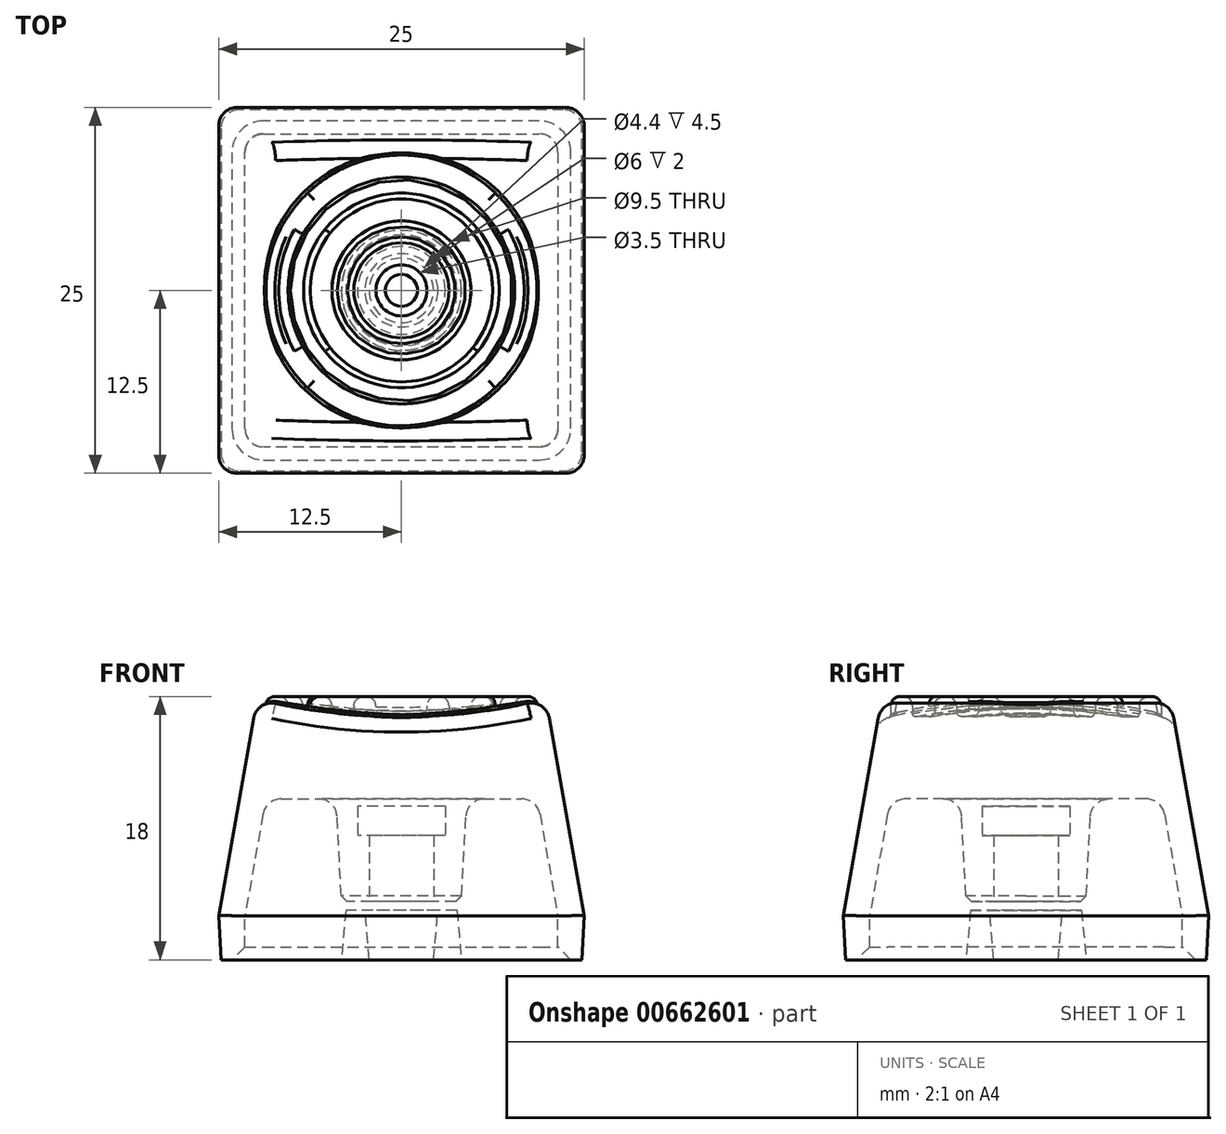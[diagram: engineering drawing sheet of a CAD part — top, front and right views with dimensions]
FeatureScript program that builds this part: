
annotation { "Feature Type Name" : "Feature", "Feature Type Description" : "" }
export const myFeature = defineFeature(function(context is Context, id is Id, definition is map)
    precondition{}
    {
        {
            var Q0;
            Q0=qCreatedBy(makeId("Top.planeOp"),FACE);
            var sketch = newSketch(context, id + "F0", { "sketchPlane" : qUnion([Q0])});
            skLineSegment(sketch, "E0.bottom", {"start": v(12.5, 12.5) * mm, "end": v(-12.5, 12.5) * mm});
            skLineSegment(sketch, "E0.top", {"start": v(12.5, -12.5) * mm, "end": v(-12.5, -12.5) * mm});
            skLineSegment(sketch, "E0.left", {"start": v(12.5, 12.5) * mm, "end": v(12.5, -12.5) * mm});
            skLineSegment(sketch, "E0.right", {"start": v(-12.5, 12.5) * mm, "end": v(-12.5, -12.5) * mm});
            skPoint(sketch, "E0.middle", {"position": v(0, 0) * mm});
            skPoint(sketch, "E1.right.end.orphan", {"position": v(-19.05, 19.05) * mm});
            skPoint(sketch, "E1.bottom.end.orphan", {"position": v(-19.05, -19.05) * mm});
            skPoint(sketch, "E1.left.end.orphan", {"position": v(19.05, 19.05) * mm});
            skPoint(sketch, "E1.left.start.orphan", {"position": v(19.05, -19.05) * mm});
            skSolve(sketch);
        }
        {
            var Q0;
            Q0=qSketchRegion(id+"F0",true);
            extrude(context, id + "F1", {"entities" : qUnion([Q0]), "depth" : 15 * mm, "offsetDistance" : 25.4 * mm, "hasDraft" : true, "draftAngle" : 10 * degree, "draftPullDirection" : true});
        }
        {
            var Q0;
            Q0=qCreatedBy(makeId("Top.planeOp"),FACE);
            var sketch = newSketch(context, id + "F2", { "sketchPlane" : qUnion([Q0])});
            skLineSegment(sketch, "E2.bottom", {"start": v(10.7, 10.7) * mm, "end": v(-10.7, 10.7) * mm});
            skLineSegment(sketch, "E2.top", {"start": v(10.7, -10.7) * mm, "end": v(-10.7, -10.7) * mm});
            skLineSegment(sketch, "E2.left", {"start": v(10.7, 10.7) * mm, "end": v(10.7, -10.7) * mm});
            skLineSegment(sketch, "E2.right", {"start": v(-10.7, 10.7) * mm, "end": v(-10.7, -10.7) * mm});
            skPoint(sketch, "E2.middle", {"position": v(0, 0) * mm});
            skSolve(sketch);
        }
        {
            var Q0;
            Q0=qSketchRegion(id+"F2",true);
            extrude(context, id + "F3", {"entities" : qUnion([Q0]), "operationType" : NewBodyOperationType.REMOVE, "depth" : 8 * mm, "offsetDistance" : 25.4 * mm, "hasDraft" : true, "draftAngle" : 10 * degree, "draftPullDirection" : true});
        }
        {
            var Q0;
            Q0=makeQuery(id+"F3.boolean.opBoolean","COPY",EDGE,{"derivedFrom":makeQuery(id+"F3.opExtrude","CAP_EDGE",EDGE,{"disambiguationData":[OSD([sQuery(id+"F2.wireOp",EDGE,"E2.bottom")])],"isStart":false})});
            var Q1;
            Q1=makeQuery(id+"F3.boolean.opBoolean","COPY",EDGE,{"derivedFrom":makeQuery(id+"F3.opExtrude","CAP_EDGE",EDGE,{"disambiguationData":[OSD([sQuery(id+"F2.wireOp",EDGE,"E2.right")])],"isStart":false})});
            var Q2;
            Q2=makeQuery(id+"F3.boolean.opBoolean","COPY",EDGE,{"derivedFrom":makeQuery(id+"F3.opExtrude","CAP_EDGE",EDGE,{"disambiguationData":[OSD([sQuery(id+"F2.wireOp",EDGE,"E2.top")])],"isStart":false})});
            var Q3;
            Q3=makeQuery(id+"F3.boolean.opBoolean","COPY",EDGE,{"derivedFrom":makeQuery(id+"F3.opExtrude","CAP_EDGE",EDGE,{"disambiguationData":[OSD([sQuery(id+"F2.wireOp",EDGE,"E2.left")])],"isStart":false})});
            fillet(context, id + "F4", {"entities" : qUnion([Q0, Q1, Q2, Q3]), "radius" : 1.27 * mm, "tangentPropagation" : true, "allowEdgeOverflow" : false});
        }
        {
            var Q0;
            Q0=makeQuery(id+"F4.opFillet","BLEND_EDGE",EDGE,{"blendedFrom":[makeQuery(id+"F3.boolean.opBoolean","COPY",EDGE,{"derivedFrom":makeQuery(id+"F3.opExtrude","CAP_EDGE",EDGE,{"disambiguationData":[OSD([sQuery(id+"F2.wireOp",EDGE,"E2.bottom")])],"isStart":false})}),makeQuery(id+"F3.boolean.opBoolean","COPY",EDGE,{"derivedFrom":makeQuery(id+"F3.opExtrude","CAP_EDGE",EDGE,{"disambiguationData":[OSD([sQuery(id+"F2.wireOp",EDGE,"E2.right")])],"isStart":false})})],"blendedInto":[]});
            var Q1;
            Q1=makeQuery(id+"F4.opFillet","BLEND_EDGE",EDGE,{"blendedFrom":[makeQuery(id+"F3.boolean.opBoolean","COPY",EDGE,{"derivedFrom":makeQuery(id+"F3.opExtrude","CAP_EDGE",EDGE,{"disambiguationData":[OSD([sQuery(id+"F2.wireOp",EDGE,"E2.bottom")])],"isStart":false})}),makeQuery(id+"F3.boolean.opBoolean","COPY",EDGE,{"derivedFrom":makeQuery(id+"F3.opExtrude","CAP_EDGE",EDGE,{"disambiguationData":[OSD([sQuery(id+"F2.wireOp",EDGE,"E2.left")])],"isStart":false})})],"blendedInto":[]});
            var Q2;
            Q2=makeQuery(id+"F4.opFillet","BLEND_EDGE",EDGE,{"blendedFrom":[makeQuery(id+"F3.boolean.opBoolean","COPY",EDGE,{"derivedFrom":makeQuery(id+"F3.opExtrude","CAP_EDGE",EDGE,{"disambiguationData":[OSD([sQuery(id+"F2.wireOp",EDGE,"E2.top")])],"isStart":false})}),makeQuery(id+"F3.boolean.opBoolean","COPY",EDGE,{"derivedFrom":makeQuery(id+"F3.opExtrude","CAP_EDGE",EDGE,{"disambiguationData":[OSD([sQuery(id+"F2.wireOp",EDGE,"E2.left")])],"isStart":false})})],"blendedInto":[]});
            var Q3;
            Q3=makeQuery(id+"F4.opFillet","BLEND_EDGE",EDGE,{"blendedFrom":[makeQuery(id+"F3.boolean.opBoolean","COPY",EDGE,{"derivedFrom":makeQuery(id+"F3.opExtrude","CAP_EDGE",EDGE,{"disambiguationData":[OSD([sQuery(id+"F2.wireOp",EDGE,"E2.top")])],"isStart":false})}),makeQuery(id+"F3.boolean.opBoolean","COPY",EDGE,{"derivedFrom":makeQuery(id+"F3.opExtrude","CAP_EDGE",EDGE,{"disambiguationData":[OSD([sQuery(id+"F2.wireOp",EDGE,"E2.right")])],"isStart":false})})],"blendedInto":[]});
            fillet(context, id + "F5", {"entities" : qUnion([Q0, Q1, Q2, Q3]), "radius" : 1.27 * mm, "tangentPropagation" : true, "allowEdgeOverflow" : false});
        }
        {
            var Q0;
            Q0=makeQuery(id+"F0.imprint","IMPRINT",FACE,{"disambiguationData":[TD([[makeQuery(id+"F0.imprint","IMPRINT",EDGE,{"derivedFrom":sQuery(id+"F0.wireOp",EDGE,"E0.bottom")}),1.0]])]});
            extrude(context, id + "F6", {"entities" : qUnion([Q0]), "operationType" : NewBodyOperationType.ADD, "oppositeDirection" : true, "depth" : 3 * mm, "offsetDistance" : 25.4 * mm, "hasDraft" : true, "draftAngle" : 3 * degree, "draftPullDirection" : true});
        }
        {
            var Q0;
            Q0=makeQuery(id+"F2.imprint","IMPRINT",FACE,{"disambiguationData":[TD([[makeQuery(id+"F2.imprint","IMPRINT",EDGE,{"derivedFrom":sQuery(id+"F2.wireOp",EDGE,"E2.bottom")}),1.0]])]});
            extrude(context, id + "F7", {"entities" : qUnion([Q0]), "operationType" : NewBodyOperationType.REMOVE, "oppositeDirection" : true, "depth" : 25.4 * mm, "offsetDistance" : 25.4 * mm});
        }
        {
            var Q0;
            Q0=makeQuery(id+"F7.boolean.opBoolean","COPY",EDGE,{"derivedFrom":makeQuery(id+"F7.opExtrude","SWEPT_EDGE",EDGE,{"disambiguationData":[OSD([sQuery(id+"F2.wireOp",EDGE,"E2.bottom"),sQuery(id+"F2.wireOp",EDGE,"E2.right")])]})});
            var Q1;
            Q1=makeQuery(id+"F7.boolean.opBoolean","COPY",EDGE,{"derivedFrom":makeQuery(id+"F7.opExtrude","SWEPT_EDGE",EDGE,{"disambiguationData":[OSD([sQuery(id+"F2.wireOp",EDGE,"E2.top"),sQuery(id+"F2.wireOp",EDGE,"E2.right")])]})});
            var Q2;
            Q2=makeQuery(id+"F7.boolean.opBoolean","COPY",EDGE,{"derivedFrom":makeQuery(id+"F7.opExtrude","SWEPT_EDGE",EDGE,{"disambiguationData":[OSD([sQuery(id+"F2.wireOp",EDGE,"E2.bottom"),sQuery(id+"F2.wireOp",EDGE,"E2.left")])]})});
            var Q3;
            Q3=makeQuery(id+"F7.boolean.opBoolean","COPY",EDGE,{"derivedFrom":makeQuery(id+"F7.opExtrude","SWEPT_EDGE",EDGE,{"disambiguationData":[OSD([sQuery(id+"F2.wireOp",EDGE,"E2.top"),sQuery(id+"F2.wireOp",EDGE,"E2.left")])]})});
            fillet(context, id + "F8", {"entities" : qUnion([Q0, Q1, Q2, Q3]), "radius" : 1.27 * mm, "tangentPropagation" : true, "allowEdgeOverflow" : false});
        }
        {
            var Q0;
            Q0=makeQuery(id+"F6.opExtrude","SWEPT_EDGE",EDGE,{"disambiguationData":[OSD([sQuery(id+"F0.wireOp",EDGE,"E0.bottom"),sQuery(id+"F0.wireOp",EDGE,"E0.right")])]});
            var Q1;
            Q1=makeQuery(id+"F6.opExtrude","SWEPT_EDGE",EDGE,{"disambiguationData":[OSD([sQuery(id+"F0.wireOp",EDGE,"E0.bottom"),sQuery(id+"F0.wireOp",EDGE,"E0.left")])]});
            var Q2;
            Q2=makeQuery(id+"F6.opExtrude","SWEPT_EDGE",EDGE,{"disambiguationData":[OSD([sQuery(id+"F0.wireOp",EDGE,"E0.top"),sQuery(id+"F0.wireOp",EDGE,"E0.right")])]});
            var Q3;
            Q3=makeQuery(id+"F6.opExtrude","SWEPT_EDGE",EDGE,{"disambiguationData":[OSD([sQuery(id+"F0.wireOp",EDGE,"E0.top"),sQuery(id+"F0.wireOp",EDGE,"E0.left")])]});
            fillet(context, id + "F9", {"entities" : qUnion([Q0, Q1, Q2, Q3]), "radius" : 1.27 * mm, "tangentPropagation" : true, "allowEdgeOverflow" : false});
        }
        {
            var Q0;
            Q0=qCreatedBy(makeId("Front.planeOp"),FACE);
            var sketch = newSketch(context, id + "F10", { "sketchPlane" : qUnion([Q0])});
            skLineSegment(sketch, "E3", {"start": v(0, 0) * mm, "end": v(0, 51.98) * mm});
            skEllipse(sketch, "E4", {"center": v(0, 28.61) * mm, "majorRadius": 25 * mm, "minorRadius": 15 * mm, "majorAxis": v(1, 0)});
            skSolve(sketch);
        }
        {
            var Q0;
            Q0=qSketchRegion(id+"F10",true);
            extrude(context, id + "F11", {"entities" : qUnion([Q0]), "operationType" : NewBodyOperationType.REMOVE, "depth" : 34.3 * mm, "offsetDistance" : 25.4 * mm, "hasSecondDirection" : true, "secondDirectionOppositeDirection" : true, "secondDirectionDepth" : 34.3 * mm});
        }
        {
            var Q0;
            Q0=makeQuery(id+"F11.boolean.opBoolean","INTERSECT",EDGE,{"derivedFrom":[makeQuery(id+"F1.opExtrude","SWEPT_FACE",FACE,{"disambiguationData":[OSD([sQuery(id+"F0.wireOp",EDGE,"E0.top")])]}),makeQuery(id+"F11.opExtrude","SWEPT_FACE",FACE,{"disambiguationData":[OSD([sQuery(id+"F10.wireOp",EDGE,"E4")])]})]});
            var Q1;
            Q1=makeQuery(id+"F1.opExtrude","SWEPT_EDGE",EDGE,{"disambiguationData":[OSD([sQuery(id+"F0.wireOp",EDGE,"E0.top"),sQuery(id+"F0.wireOp",EDGE,"E0.right")])]});
            var Q2;
            Q2=makeQuery(id+"F11.boolean.opBoolean","INTERSECT",EDGE,{"derivedFrom":[makeQuery(id+"F1.opExtrude","SWEPT_FACE",FACE,{"disambiguationData":[OSD([sQuery(id+"F0.wireOp",EDGE,"E0.right")])]}),makeQuery(id+"F11.opExtrude","SWEPT_FACE",FACE,{"disambiguationData":[OSD([sQuery(id+"F10.wireOp",EDGE,"E4")])]})]});
            var Q3;
            Q3=makeQuery(id+"F1.opExtrude","SWEPT_EDGE",EDGE,{"disambiguationData":[OSD([sQuery(id+"F0.wireOp",EDGE,"E0.top"),sQuery(id+"F0.wireOp",EDGE,"E0.left")])]});
            var Q4;
            Q4=makeQuery(id+"F11.boolean.opBoolean","INTERSECT",EDGE,{"derivedFrom":[makeQuery(id+"F1.opExtrude","SWEPT_FACE",FACE,{"disambiguationData":[OSD([sQuery(id+"F0.wireOp",EDGE,"E0.left")])]}),makeQuery(id+"F11.opExtrude","SWEPT_FACE",FACE,{"disambiguationData":[OSD([sQuery(id+"F10.wireOp",EDGE,"E4")])]})]});
            var Q5;
            Q5=makeQuery(id+"F1.opExtrude","SWEPT_EDGE",EDGE,{"disambiguationData":[OSD([sQuery(id+"F0.wireOp",EDGE,"E0.bottom"),sQuery(id+"F0.wireOp",EDGE,"E0.left")])]});
            var Q6;
            Q6=makeQuery(id+"F11.boolean.opBoolean","INTERSECT",EDGE,{"derivedFrom":[makeQuery(id+"F1.opExtrude","SWEPT_FACE",FACE,{"disambiguationData":[OSD([sQuery(id+"F0.wireOp",EDGE,"E0.bottom")])]}),makeQuery(id+"F11.opExtrude","SWEPT_FACE",FACE,{"disambiguationData":[OSD([sQuery(id+"F10.wireOp",EDGE,"E4")])]})]});
            var Q7;
            Q7=makeQuery(id+"F1.opExtrude","SWEPT_EDGE",EDGE,{"disambiguationData":[OSD([sQuery(id+"F0.wireOp",EDGE,"E0.bottom"),sQuery(id+"F0.wireOp",EDGE,"E0.right")])]});
            fillet(context, id + "F12", {"entities" : qUnion([Q0, Q1, Q2, Q3, Q4, Q5, Q6, Q7]), "radius" : 1.27 * mm, "tangentPropagation" : true, "allowEdgeOverflow" : false});
        }
        {
            var Q0;
            Q0=makeQuery(id+"F7.boolean.opBoolean","INTERSECT",EDGE,{"derivedFrom":[makeQuery(id+"F6.opExtrude","CAP_FACE",FACE,{"disambiguationData":[OSD([sQuery(id+"F0.wireOp",EDGE,"E0.bottom"),sQuery(id+"F0.wireOp",EDGE,"E0.top"),sQuery(id+"F0.wireOp",EDGE,"E0.left"),sQuery(id+"F0.wireOp",EDGE,"E0.right")])],"isStart":false}),makeQuery(id+"F7.opExtrude","SWEPT_FACE",FACE,{"disambiguationData":[OSD([sQuery(id+"F2.wireOp",EDGE,"E2.top")])]})]});
            chamfer(context, id + "F13", {"entities" : qUnion([Q0]), "width" : .889 * mm, "tangentPropagation" : true});
        }
        {
            var Q0;
            Q0=qCreatedBy(makeId("Top.planeOp"),FACE);
            cPlane(context, id + "F14", {"entities" : qUnion([Q0]), "cplaneType" : CPlaneType.OFFSET, "offset" : 1 * mm, "width" : 150 * mm, "height" : 150 * mm});
        }
        {
            var Q0;
            Q0=qCreatedBy(id+"F14.planeOp",FACE);
            var sketch = newSketch(context, id + "F15", { "sketchPlane" : qUnion([Q0])});
            skCircle(sketch, "E5", {"center": v(0, 0) * mm, "radius": 4.1 * mm});
            skSolve(sketch);
        }
        {
            var Q0;
            Q0=qSketchRegion(id+"F15",true);
            extrude(context, id + "F16", {"entities" : qUnion([Q0]), "operationType" : NewBodyOperationType.ADD, "depth" : 8.9 * mm, "offsetDistance" : 25.4 * mm, "hasDraft" : true, "draftAngle" : 3 * degree, "hasSecondDirectionDraft" : true, "secondDirectionDraftAngle" : 3 * degree, "secondDirectionDraftPullDirection" : true});
        }
        {
            var Q0;
            Q0=makeQuery(id+"F16.boolean.opBoolean","INTERSECT",EDGE,{"derivedFrom":[makeQuery(id+"F3.boolean.opBoolean","COPY",FACE,{"derivedFrom":makeQuery(id+"F3.opExtrude","CAP_FACE",FACE,{"disambiguationData":[OSD([sQuery(id+"F2.wireOp",EDGE,"E2.bottom"),sQuery(id+"F2.wireOp",EDGE,"E2.top"),sQuery(id+"F2.wireOp",EDGE,"E2.left"),sQuery(id+"F2.wireOp",EDGE,"E2.right")])],"isStart":false})}),makeQuery(id+"F16.opExtrude","SWEPT_FACE",FACE,{"disambiguationData":[OSD([sQuery(id+"F15.wireOp",EDGE,"E5")])]})]});
            fillet(context, id + "F17", {"entities" : qUnion([Q0]), "radius" : 1.27 * mm, "tangentPropagation" : true, "allowEdgeOverflow" : false});
        }
        {
            var Q0;
            Q0=qCreatedBy(id+"F14.planeOp",FACE);
            var sketch = newSketch(context, id + "F18", { "sketchPlane" : qUnion([Q0])});
            skCircle(sketch, "E6", {"center": v(0, 0) * mm, "radius": 2.2 * mm});
            skSolve(sketch);
        }
        {
            var Q0;
            Q0=qSketchRegion(id+"F18",true);
            extrude(context, id + "F19", {"entities" : qUnion([Q0]), "operationType" : NewBodyOperationType.REMOVE, "depth" : 4.5 * mm, "offsetDistance" : 25 * mm});
        }
        {
            var Q0;
            Q0=qCreatedBy(id+"F14.planeOp",FACE);
            cPlane(context, id + "F20", {"entities" : qUnion([Q0]), "cplaneType" : CPlaneType.OFFSET, "offset" : 4.5 * mm, "width" : 150 * mm, "height" : 150 * mm});
        }
        {
            var Q0;
            Q0=qCreatedBy(id+"F20.planeOp",FACE);
            var sketch = newSketch(context, id + "F21", { "sketchPlane" : qUnion([Q0])});
            skCircle(sketch, "E7", {"center": v(0, 0) * mm, "radius": 3 * mm});
            skSolve(sketch);
        }
        {
            var Q0;
            Q0=qSketchRegion(id+"F21",true);
            extrude(context, id + "F22", {"entities" : qUnion([Q0]), "operationType" : NewBodyOperationType.REMOVE, "depth" : 2 * mm, "offsetDistance" : 25 * mm});
        }
        {
            var Q0;
            Q0=makeQuery(id+"F16.opExtrude","CAP_EDGE",EDGE,{"disambiguationData":[OSD([sQuery(id+"F15.wireOp",EDGE,"E5")])],"isStart":true});
            chamfer(context, id + "F23", {"entities" : qUnion([Q0]), "width" : .4 * mm, "tangentPropagation" : true});
        }
        {
            var Q0;
            Q0=qCreatedBy(makeId("Top.planeOp"),FACE);
            cPlane(context, id + "F24", {"entities" : qUnion([Q0]), "cplaneType" : CPlaneType.OFFSET, "offset" : 11 * mm, "width" : 150 * mm, "height" : 150 * mm});
        }
        {
            var Q0;
            Q0=qCreatedBy(id+"F24.planeOp",FACE);
            var sketch = newSketch(context, id + "F25", { "sketchPlane" : qUnion([Q0])});
            skCircle(sketch, "E8", {"center": v(0, 0) * mm, "radius": 1.75 * mm});
            skCircle(sketch, "E9", {"center": v(0, 0) * mm, "radius": 3.25 * mm});
            skCircle(sketch, "E10", {"center": v(0, 0) * mm, "radius": 4.75 * mm});
            skCircle(sketch, "E11", {"center": v(0, 0) * mm, "radius": 6.25 * mm});
            skCircle(sketch, "E12", {"center": v(0, 0) * mm, "radius": 7.75 * mm});
            skCircle(sketch, "E13", {"center": v(0, 0) * mm, "radius": 9.25 * mm});
            skSolve(sketch);
        }
        {
            var Q0;
            Q0 = qSketchRegion(id + "F25", true);
            var Q1;
            Q1=makeQuery(id+"F25.imprint","IMPRINT",FACE,{"disambiguationData":[TD([[makeQuery(id+"F25.imprint","IMPRINT",EDGE,{"derivedFrom":sQuery(id+"F25.wireOp",EDGE,"E10")}),-1.0]])]});
            var Q2;
            Q2=makeQuery(id+"F25.imprint","IMPRINT",FACE,{"disambiguationData":[TD([[makeQuery(id+"F25.imprint","IMPRINT",EDGE,{"derivedFrom":sQuery(id+"F25.wireOp",EDGE,"E8")}),-1.0]])]});
            extrude(context, id + "F26", {"entities" : qUnion([Q0, Q1, Q2]), "depth" : 4 * mm, "offsetDistance" : 25 * mm});
        }
        {
            var Q0;
            Q0=makeQuery(id+"F1.opExtrude","SWEPT_BODY",BODY,{"disambiguationData":[OSD([sQuery(id+"F0.wireOp",EDGE,"E0.bottom"),sQuery(id+"F0.wireOp",EDGE,"E0.top"),sQuery(id+"F0.wireOp",EDGE,"E0.left"),sQuery(id+"F0.wireOp",EDGE,"E0.right")])]});
            var Q1;
            Q1=makeQuery(id+"F26.opExtrude","SWEPT_BODY",BODY,{"disambiguationData":[OSD([sQuery(id+"F25.wireOp",EDGE,"E12"),sQuery(id+"F25.wireOp",EDGE,"E13")])]});
            var Q2;
            Q2=makeQuery(id+"F26.opExtrude","SWEPT_BODY",BODY,{"disambiguationData":[OSD([sQuery(id+"F25.wireOp",EDGE,"E10"),sQuery(id+"F25.wireOp",EDGE,"E11")])]});
            var Q3;
            Q3=makeQuery(id+"F26.opExtrude","SWEPT_BODY",BODY,{"disambiguationData":[OSD([sQuery(id+"F25.wireOp",EDGE,"E8"),sQuery(id+"F25.wireOp",EDGE,"E9")])]});
            booleanBodies(context, id + "F27", {"operationType" : BooleanOperationType.UNION, "tools" : qUnion([Q0, Q1, Q2, Q3])});
        }
        {
            var Q0;
            Q0=makeQuery(id+"F27.opBoolean","INTERSECT",EDGE,{"disambiguationData":[OD(3.0)],"derivedFrom":[makeQuery(id+"F11.boolean.opBoolean","COPY",FACE,{"derivedFrom":makeQuery(id+"F11.opExtrude","SWEPT_FACE",FACE,{"disambiguationData":[OSD([sQuery(id+"F10.wireOp",EDGE,"E4")])]})}),makeQuery(id+"F26.opExtrude","SWEPT_FACE",FACE,{"disambiguationData":[OSD([sQuery(id+"F25.wireOp",EDGE,"E13")])]})]});
            var Q1;
            Q1=makeQuery(id+"F27.opBoolean","INTERSECT",EDGE,{"derivedFrom":[makeQuery(id+"F11.boolean.opBoolean","COPY",FACE,{"derivedFrom":makeQuery(id+"F11.opExtrude","SWEPT_FACE",FACE,{"disambiguationData":[OSD([sQuery(id+"F10.wireOp",EDGE,"E4")])]})}),makeQuery(id+"F26.opExtrude","SWEPT_FACE",FACE,{"disambiguationData":[OSD([sQuery(id+"F25.wireOp",EDGE,"E12")])]})]});
            fillet(context, id + "F28", {"entities" : qUnion([Q0, Q1]), "radius" : .2 * mm, "tangentPropagation" : true, "allowEdgeOverflow" : false});
        }
        {
            var Q0;
            Q0=makeQuery(id+"F26.opExtrude","CAP_EDGE",EDGE,{"disambiguationData":[OSD([sQuery(id+"F25.wireOp",EDGE,"E13")])],"isStart":false});
            var Q1;
            Q1=makeQuery(id+"F26.opExtrude","CAP_EDGE",EDGE,{"disambiguationData":[OSD([sQuery(id+"F25.wireOp",EDGE,"E12")])],"isStart":false});
            var Q2;
            Q2=makeQuery(id+"F26.opExtrude","CAP_EDGE",EDGE,{"disambiguationData":[OSD([sQuery(id+"F25.wireOp",EDGE,"E11")])],"isStart":false});
            var Q3;
            Q3=makeQuery(id+"F26.opExtrude","CAP_EDGE",EDGE,{"disambiguationData":[OSD([sQuery(id+"F25.wireOp",EDGE,"E10")])],"isStart":false});
            var Q4;
            Q4=makeQuery(id+"F26.opExtrude","CAP_EDGE",EDGE,{"disambiguationData":[OSD([sQuery(id+"F25.wireOp",EDGE,"E9")])],"isStart":false});
            var Q5;
            Q5=makeQuery(id+"F26.opExtrude","CAP_EDGE",EDGE,{"disambiguationData":[OSD([sQuery(id+"F25.wireOp",EDGE,"E8")])],"isStart":false});
            var Q6;
            Q6=makeQuery(id+"F27.opBoolean","INTERSECT",EDGE,{"derivedFrom":[makeQuery(id+"F11.boolean.opBoolean","COPY",FACE,{"derivedFrom":makeQuery(id+"F11.opExtrude","SWEPT_FACE",FACE,{"disambiguationData":[OSD([sQuery(id+"F10.wireOp",EDGE,"E4")])]})}),makeQuery(id+"F26.opExtrude","SWEPT_FACE",FACE,{"disambiguationData":[OSD([sQuery(id+"F25.wireOp",EDGE,"E8")])]})]});
            fillet(context, id + "F29", {"entities" : qUnion([Q0, Q1, Q2, Q3, Q4, Q5, Q6]), "radius" : .66 * mm, "tangentPropagation" : true, "allowEdgeOverflow" : false});
        }
        {
            var Q0;
            Q0=makeQuery(id+"F27.opBoolean","INTERSECT",EDGE,{"derivedFrom":[makeQuery(id+"F11.boolean.opBoolean","COPY",FACE,{"derivedFrom":makeQuery(id+"F11.opExtrude","SWEPT_FACE",FACE,{"disambiguationData":[OSD([sQuery(id+"F10.wireOp",EDGE,"E4")])]})}),makeQuery(id+"F26.opExtrude","SWEPT_FACE",FACE,{"disambiguationData":[OSD([sQuery(id+"F25.wireOp",EDGE,"E10")])]})]});
            var Q1;
            Q1=makeQuery(id+"F27.opBoolean","INTERSECT",EDGE,{"derivedFrom":[makeQuery(id+"F11.boolean.opBoolean","COPY",FACE,{"derivedFrom":makeQuery(id+"F11.opExtrude","SWEPT_FACE",FACE,{"disambiguationData":[OSD([sQuery(id+"F10.wireOp",EDGE,"E4")])]})}),makeQuery(id+"F26.opExtrude","SWEPT_FACE",FACE,{"disambiguationData":[OSD([sQuery(id+"F25.wireOp",EDGE,"E11")])]})]});
            var Q2;
            Q2=makeQuery(id+"F27.opBoolean","INTERSECT",EDGE,{"derivedFrom":[makeQuery(id+"F11.boolean.opBoolean","COPY",FACE,{"derivedFrom":makeQuery(id+"F11.opExtrude","SWEPT_FACE",FACE,{"disambiguationData":[OSD([sQuery(id+"F10.wireOp",EDGE,"E4")])]})}),makeQuery(id+"F26.opExtrude","SWEPT_FACE",FACE,{"disambiguationData":[OSD([sQuery(id+"F25.wireOp",EDGE,"E9")])]})]});
            fillet(context, id + "F30", {"entities" : qUnion([Q0, Q1, Q2]), "radius" : .4 * mm, "tangentPropagation" : true, "allowEdgeOverflow" : false});
        }
        {
            var Q0;
            Q0=qCreatedBy(makeId("Top.planeOp"),FACE);
            cPlane(context, id + "F31", {"entities" : qUnion([Q0]), "cplaneType" : CPlaneType.OFFSET, "offset" : 3 * mm, "oppositeDirection" : true, "width" : 150 * mm, "height" : 150 * mm});
        }
        {
            var Q0;
            Q0=qCreatedBy(id+"F31.planeOp",FACE);
            var sketch = newSketch(context, id + "F32", { "sketchPlane" : qUnion([Q0])});
            skCircle(sketch, "E14", {"center": v(0, 0) * mm, "radius": 2.2 * mm});
            skCircle(sketch, "E15", {"center": v(0, 0) * mm, "radius": 4.1 * mm});
            skSolve(sketch);
        }
        {
            var Q0;
            Q0 = qSketchRegion(id + "F32", true);
            extrude(context, id + "F33", {"entities" : qUnion([Q0]), "depth" : 3.4 * mm, "offsetDistance" : 25 * mm, "hasDraft" : true, "draftAngle" : 5 * degree, "draftPullDirection" : true});
        }
    });
